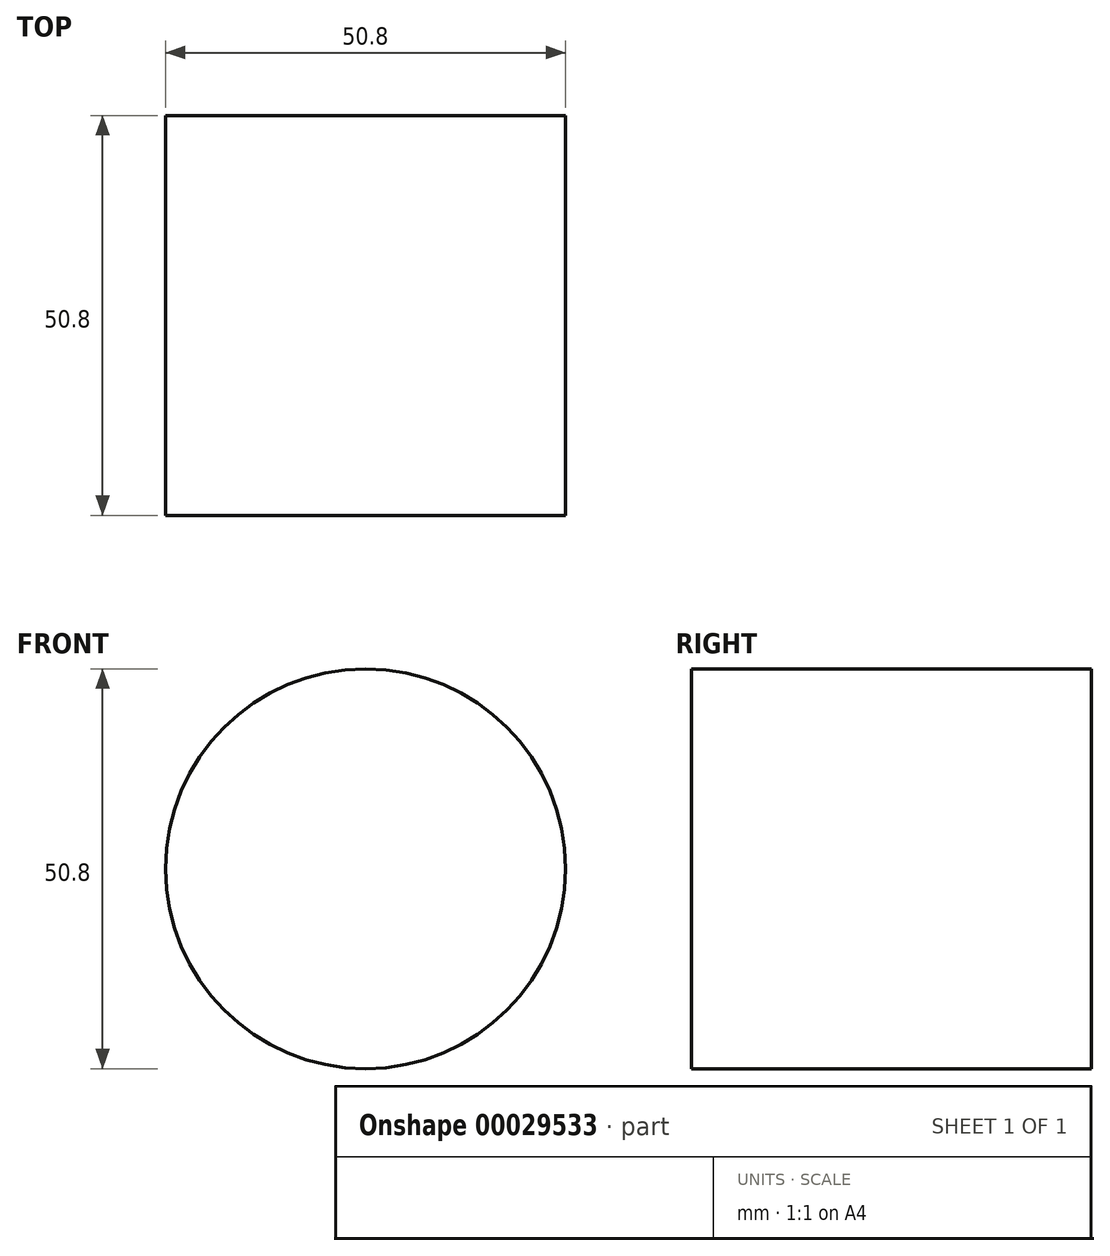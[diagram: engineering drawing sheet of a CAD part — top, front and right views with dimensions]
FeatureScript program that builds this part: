
annotation { "Feature Type Name" : "Feature", "Feature Type Description" : "" }
export const myFeature = defineFeature(function(context is Context, id is Id, definition is map)
    precondition{}
    {
        {
            var Q0;
            Q0=qCreatedBy(makeId("Front.planeOp"),FACE);
            var sketch = newSketch(context, id + "F0", { "sketchPlane" : qUnion([Q0])});
            skCircle(sketch, "E0", {"center": v(0, 0) * mm, "radius": 25.4 * mm});
            skSolve(sketch);
        }
        {
            var Q0;
            Q0=makeQuery(id+"F0.imprint","IMPRINT",FACE,{"disambiguationData":[TD([[makeQuery(id+"F0.imprint","IMPRINT",EDGE,{"derivedFrom":sQuery(id+"F0.wireOp",EDGE,"E0")}),1.0]])]});
            extrude(context, id + "F1", {"entities" : qUnion([Q0]), "depth" : 50.8 * mm});
        }
    });
